# Revit family: Valve-Flushometer-Kohler-Tripoint-K_10956
name_source: partatom
category: Plumbing Fixtures
revit_build: Autodesk Revit 2015 (Build: 20140606_1530(x64)
units: mm (PartAtom-declared; Revit-internal decimal feet)

## types (1)
- CP-Polished Chrome
    ADA Compliant = Yes
    Assembly Code = D2020300
    CW Connection = Yes
    CWFU = 0
    Cold Water Connector = IPS Supply
    Cold Water Diameter = 1"
    Cold Water Radius = 0' - 0 1/2"
    Critical Level Above Fixture = 0' - 6"
    Default Elevation = 4' - 0"
    Description = 1.28 GPF WC Flushometer
    Finish = Metal - Kohler - CP - Polished Chrome
    Fixture Pressure Max (Static) = 80 psi (551.6 kPa)
    Flow Rate = 25.00 GPM
    Flush Rate = 1.28 gpf
    HW Connection = No
    HWFU = 0
    Height = 1' - 4 3/4"
    Keynote = 22 40 00
    Manufacturer = Kohler
    Material = Brass
    Model = K-10956-SV
    Power Source = AA 1.5 V, included
    Product Documentation Link = http://www.us.kohler.com
    Product Name = Tripoint™ DC 1.28 GPF WC Flushometer
    Product Page URL = http://www.us.kohler.com
    URL = http://www.us.kohler.com
    Vent Connection = No
    Version = 2014 - v1.0a
    WFU = 0
    Waste Connection = No
    Width = 0' - 5"

## geometry (parser evidence)
native form markers: Sweep x5
no freeform markers — native parametric forms only
